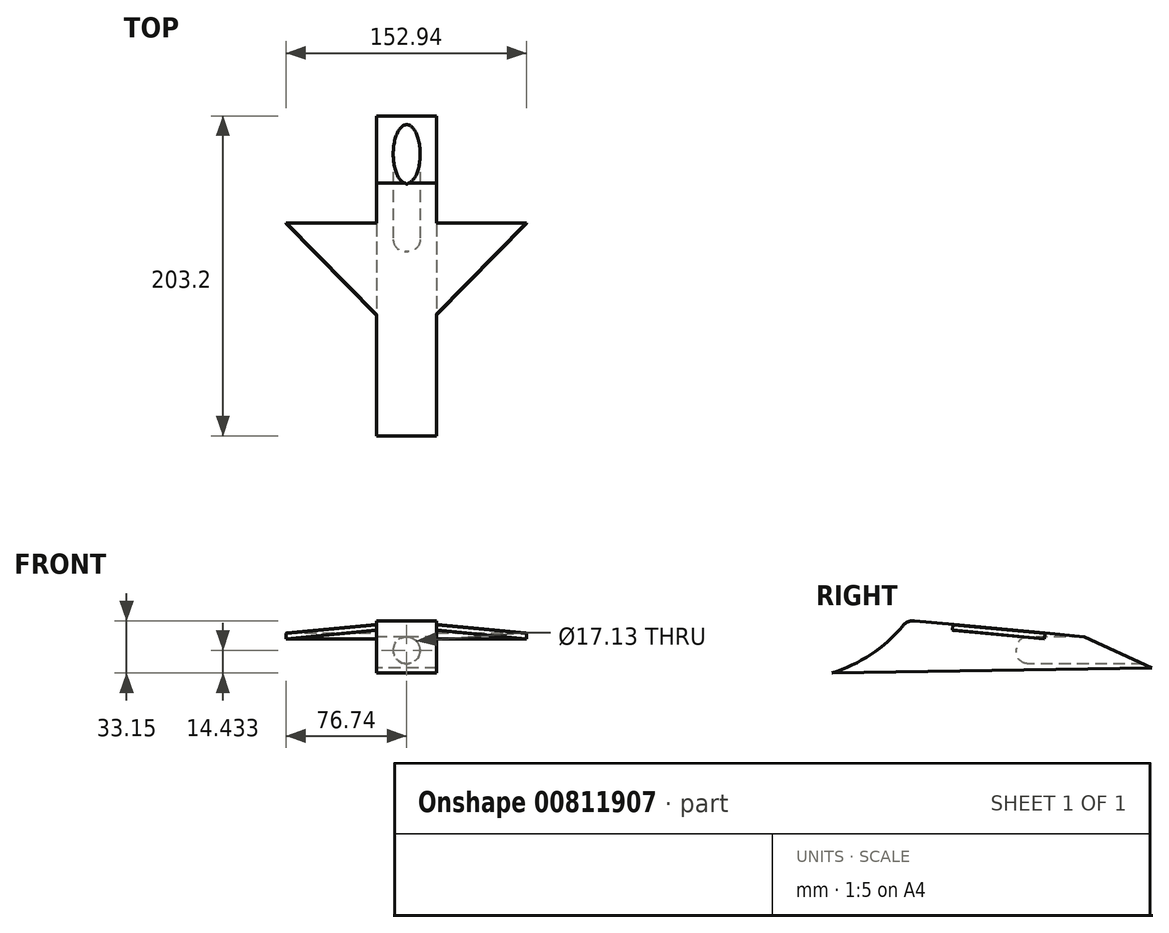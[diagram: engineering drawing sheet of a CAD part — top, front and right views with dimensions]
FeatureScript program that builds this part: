
annotation { "Feature Type Name" : "Feature", "Feature Type Description" : "" }
export const myFeature = defineFeature(function(context is Context, id is Id, definition is map)
    precondition{}
    {
        {
            var Q0;
            Q0=qCreatedBy(makeId("Right.planeOp"),FACE);
            var sketch = newSketch(context, id + "F0", { "sketchPlane" : qUnion([Q0])});
            skArc(sketch, "E0", {"start": v(-117.1, -22.95) * mm, "mid": v(-90.57, -9.92) * mm, "end": v(-69.3, 10.6) * mm});
            skLineSegment(sketch, "E1", {"start": v(-69.3, 10.6) * mm, "end": v(43.35, 0) * mm});
            skLineSegment(sketch, "E2", {"start": v(43.35, 0) * mm, "end": v(86.1, -19.62) * mm});
            skLineSegment(sketch, "E3", {"start": v(86.1, -19.62) * mm, "end": v(-117.1, -22.95) * mm});
            skSolve(sketch);
        }
        {
            var Q0;
            Q0 = qSketchRegion(id + "F0", true);
            extrude(context, id + "F1", {"entities" : qUnion([Q0]), "depth" : 19.05 * mm, "offsetDistance" : 25.4 * mm, "hasSecondDirection" : true, "secondDirectionOppositeDirection" : true, "secondDirectionDepth" : 19.05 * mm});
        }
        {
            var Q0;
            Q0=makeQuery(id+"F1.opExtrude","SWEPT_EDGE",EDGE,{"disambiguationData":[OSD([sQuery(id+"F0.wireOp",EDGE,"E0"),sQuery(id+"F0.wireOp",EDGE,"E1")])]});
            fillet(context, id + "F2", {"entities" : qUnion([Q0]), "radius" : 8.77 * mm, "tangentPropagation" : true, "allowEdgeOverflow" : false});
        }
        {
            var Q0;
            Q0=makeQuery(id+"F1.opExtrude","SWEPT_FACE",FACE,{"disambiguationData":[OSD([sQuery(id+"F0.wireOp",EDGE,"E1")])]});
            var sketch = newSketch(context, id + "F3", { "sketchPlane" : qUnion([Q0])});
            skLineSegment(sketch, "E4", {"start": v(0, -60.16) * mm, "end": v(-76.74, 17.76) * mm});
            skLineSegment(sketch, "E5", {"start": v(-76.74, 17.76) * mm, "end": v(0, 17.76) * mm});
            skLineSegment(sketch, "E6", {"start": v(0, 17.76) * mm, "end": v(0, -60.16) * mm});
            skLineSegment(sketch, "E7", {"start": v(0, -60.16) * mm, "end": v(76.2, 17.76) * mm});
            skLineSegment(sketch, "E8", {"start": v(76.2, 17.76) * mm, "end": v(0, 17.76) * mm});
            skSolve(sketch);
        }
        {
            var Q0;
            Q0 = qSketchRegion(id + "F3", true);
            extrude(context, id + "F4", {"entities" : qUnion([Q0]), "operationType" : NewBodyOperationType.ADD, "oppositeDirection" : true, "depth" : 3.8 * mm, "offsetDistance" : 25.4 * mm});
        }
        {
            var Q0;
            Q0=makeQuery(id+"F4.opExtrude","CAP_EDGE",EDGE,{"disambiguationData":[OSD([sQuery(id+"F3.wireOp",EDGE,"E7")])],"isStart":false});
            var Q1;
            Q1=makeQuery(id+"F4.opExtrude","CAP_EDGE",EDGE,{"disambiguationData":[OSD([sQuery(id+"F3.wireOp",EDGE,"E7")])],"isStart":true});
            var Q2;
            Q2=makeQuery(id+"F4.opExtrude","CAP_EDGE",EDGE,{"disambiguationData":[OSD([sQuery(id+"F3.wireOp",EDGE,"E4")])],"isStart":true});
            var Q3;
            Q3=makeQuery(id+"F4.opExtrude","CAP_EDGE",EDGE,{"disambiguationData":[OSD([sQuery(id+"F3.wireOp",EDGE,"E4")])],"isStart":false});
            chamfer(context, id + "F5", {"entities" : qUnion([Q0, Q1, Q2, Q3]), "width" : 0.25 * mm, "tangentPropagation" : true});
        }
        {
            var Q0;
            Q0=qCreatedBy(makeId("Front.planeOp"),FACE);
            var sketch = newSketch(context, id + "F6", { "sketchPlane" : qUnion([Q0])});
            skCircle(sketch, "E9", {"center": v(0, -8.52) * mm, "radius": 8.56 * mm});
            skSolve(sketch);
        }
        {
            var Q0;
            Q0 = qSketchRegion(id + "F6", true);
            extrude(context, id + "F7", {"entities" : qUnion([Q0]), "operationType" : NewBodyOperationType.REMOVE, "oppositeDirection" : true, "depth" : 131.83 * mm, "offsetDistance" : 25.4 * mm});
        }
        {
            var Q0;
            Q0=makeQuery(id+"F7.boolean.opBoolean","COPY",EDGE,{"derivedFrom":makeQuery(id+"F7.opExtrude","CAP_EDGE",EDGE,{"disambiguationData":[OSD([sQuery(id+"F6.wireOp",EDGE,"E9")])],"isStart":true})});
            fillet(context, id + "F8", {"entities" : qUnion([Q0]), "radius" : 7.62 * mm, "tangentPropagation" : true, "allowEdgeOverflow" : false});
        }
    });
